# Revit family: Nero Sconce 3-584-xx
name_source: partatom
category: Luminarias
units: mm (PartAtom-declared; Revit-internal decimal feet)

## family parameters
Anfitrión = Muro
Compartido = No
Corte con vacíos al cargar = No
Cota de conector redondo = Diámetro de uso
Número OmniClass = 23.80.70.00
Origen de luz = Sí
Punto de cálculo de habitación = No
Siempre vertical = Sí
Tipo de pieza = Normal
Título OmniClass = Lighting

## types (1)
- 3-584-1540 / Black - White Frost Glass
    Archivo de red fotométrica = 3-584-1540 Nero Sconce.ies
    Cambio de temperatura de color de luz atenuada = <Ninguno>
    Comentarios de vataje = 16.14W at 120V
    Elevación por defecto = 0 "
    Fabricante = Oxygen - Lighting & Fans
    Filtro de color = 16777215
    Lámpara = LED array
    Main Diffuser = White Frost Glass
    Metal Finish = 15 - Black
    Metal Finish 2 = 40 - Aged Brass
    Modelo = 3-584-xx Nero Wall Lantern
    References = Ref. 3 = 120 V / Ref. 37 = 277 V
    URL = www.oxygenlighting.com
    Voltage = 120 V
    Voltage Input = 120 V or 277 V - 50/60 Hz
    Ángulo de inclinación = 0.00°

## geometry (parser evidence)
native form markers: Blend x2, Sweep x4
no freeform markers — native parametric forms only
